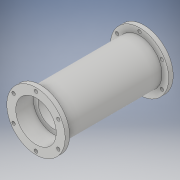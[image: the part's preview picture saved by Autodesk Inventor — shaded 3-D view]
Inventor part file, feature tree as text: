
AUTODESK INVENTOR PART (.ipt)
format: ipt  version: 2017 (Build 210142000, 142)  size: 167,424 bytes
history: native  units: in
note: dims shown in document units (in); Inventor stores cm internally (conversion verified against a paired STEP export)
features: extrude x8, sketch x8
ambient origin geometry x8: Origin, YZ Plane, XZ Plane, XY Plane, X Axis, Y Axis, Z Axis, Center Point
bodies: Solid1 (feature_tree)
feature tree (16):
  extrude  "Extrusion1"  Depth=6.0in TaperAngle=0.0deg
  extrude  "Extrusion2"  Depth=6.0in TaperAngle=0.0deg
  extrude  "Extrusion3"  Depth=0.98in TaperAngle=0.0deg
  extrude  "Extrusion4"  Depth=1.02in TaperAngle=0.0deg
  extrude  "Extrusion5"  Depth=7.0in TaperAngle=0.0deg
  extrude  "Extrusion6"  Depth=0.25in TaperAngle=0.0deg
  extrude  "Extrusion7"  Depth=0.25in
  extrude  "Extrusion8"  Depth=7.0in TaperAngle=0.0deg
  sketch  "Sketch1"  dims[d0=3.24in d1=6.0in d2=0.0in]
  sketch  "Sketch2"  dims[d3=1.73in d4=6.0in d5=0.0in]
  sketch  "Sketch3"  dims[d6=2.25in d7=0.98in d8=0.0in]
  sketch  "Sketch4"  dims[d9=2.25in d10=1.02in d11=0.0in]
  sketch  "Sketch5"  dims[d12=2.5in d13=7.0in d14=0.0in]
  sketch  "Sketch6"  dims[d15=3.24in d16=0.25in d17=0.0in]
  sketch  "Sketch7"  dims[d18=0.25in d19=0.0in d20=0.1875in]
  sketch  "Sketch8"  dims[d21=2.3622in d23=360.0deg d25=7.0in d26=0.0in]
